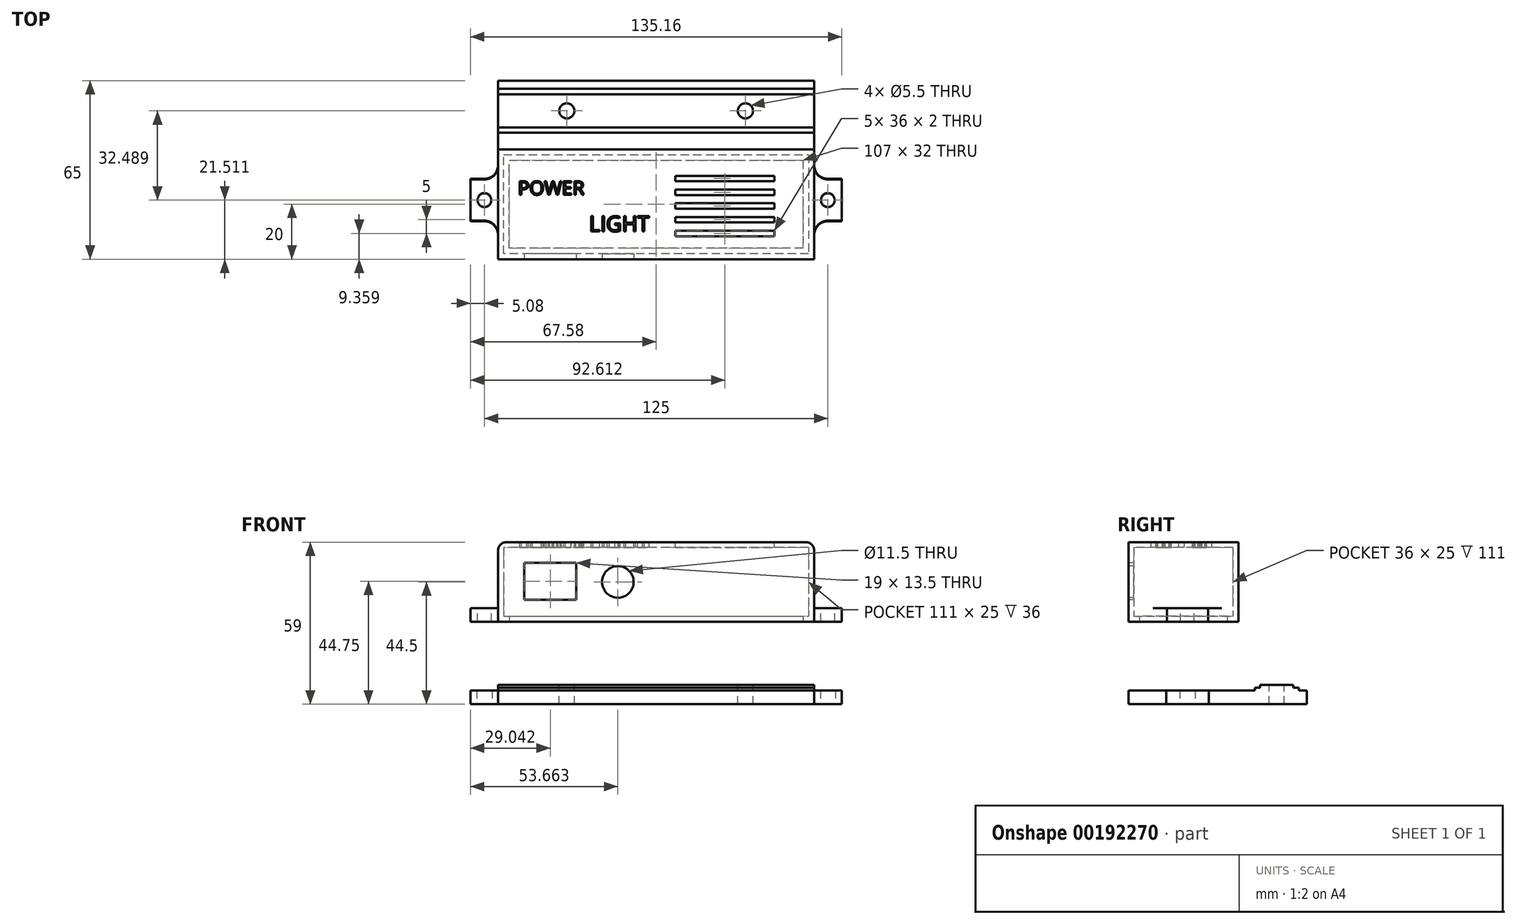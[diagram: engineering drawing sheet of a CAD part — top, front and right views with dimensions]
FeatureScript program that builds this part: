
annotation { "Feature Type Name" : "Feature", "Feature Type Description" : "" }
export const myFeature = defineFeature(function(context is Context, id is Id, definition is map)
    precondition{}
    {
        {
            var Q0;
            Q0=qCreatedBy(makeId("Top.planeOp"),FACE);
            var sketch = newSketch(context, id + "F0", { "sketchPlane" : qUnion([Q0])});
            skLineSegment(sketch, "E0", {"start": v(0, 0) * mm, "end": v(0, 40) * mm});
            skLineSegment(sketch, "E1", {"start": v(0, 40) * mm, "end": v(115, 40) * mm});
            skLineSegment(sketch, "E2", {"start": v(115, 40) * mm, "end": v(115, 0) * mm});
            skLineSegment(sketch, "E3", {"start": v(115, 0) * mm, "end": v(0, 0) * mm});
            skPoint(sketch, "E4.endSnap0", {"position": v(0, 20) * mm});
            skLineSegment(sketch, "E5", {"start": v(-10, 20) * mm, "end": v(-10, 29) * mm});
            skLineSegment(sketch, "E6", {"start": v(-10, 29) * mm, "end": v(0, 29) * mm});
            skLineSegment(sketch, "E7", {"start": v(0, 29) * mm, "end": v(0, 14) * mm});
            skLineSegment(sketch, "E8", {"start": v(0, 14) * mm, "end": v(-10, 14) * mm});
            skLineSegment(sketch, "E9", {"start": v(-10, 14) * mm, "end": v(-10, 20) * mm});
            skLineSegment(sketch, "E10", {"start": v(125, 15) * mm, "end": v(125, 29) * mm});
            skLineSegment(sketch, "E11", {"start": v(125, 29) * mm, "end": v(115, 29) * mm});
            skLineSegment(sketch, "E12", {"start": v(115, 29) * mm, "end": v(115, 14) * mm});
            skLineSegment(sketch, "E13", {"start": v(115, 14) * mm, "end": v(125, 14) * mm});
            skLineSegment(sketch, "E14", {"start": v(125, 14) * mm, "end": v(125, 15) * mm});
            skLineSegment(sketch, "E15.0", {"start": v(2, 2) * mm, "end": v(2, 38) * mm});
            skLineSegment(sketch, "E15.1", {"start": v(113, 2) * mm, "end": v(2, 2) * mm});
            skLineSegment(sketch, "E15.2", {"start": v(113, 38) * mm, "end": v(113, 2) * mm});
            skLineSegment(sketch, "E15.3", {"start": v(2, 38) * mm, "end": v(113, 38) * mm});
            skSolve(sketch);
        }
        {
            var Q0;
            {var subQ5=sQuery(id+"F0.wireOp",EDGE,"E1");Q0=makeQuery(id+"F0.imprint","IMPRINT",FACE,{"disambiguationData":[TD([[makeQuery(id+"F0.imprint","IMPRINT",EDGE,{"derivedFrom":subQ5}),-1.0]])]});}
            extrude(context, id + "F1", {"entities" : qUnion([Q0]), "depth" : 25 * mm});
        }
        {
            var Q0;
            Q0=makeQuery(id+"F0.imprint","IMPRINT",FACE,{"disambiguationData":[TD([[makeQuery(id+"F0.imprint","IMPRINT",EDGE,{"derivedFrom":sQuery(id+"F0.wireOp",EDGE,"E5")}),-1.0]])]});
            var Q1;
            Q1=makeQuery(id+"F0.imprint","IMPRINT",FACE,{"disambiguationData":[TD([[makeQuery(id+"F0.imprint","IMPRINT",EDGE,{"derivedFrom":sQuery(id+"F0.wireOp",EDGE,"E10")}),1.0]])]});
            extrude(context, id + "F2", {"entities" : qUnion([Q0, Q1]), "operationType" : NewBodyOperationType.ADD, "depth" : 3 * mm});
        }
        {
            var Q0;
            Q0=makeQuery(id+"F1.opExtrude","CAP_FACE",FACE,{"disambiguationData":[OSD([sQuery(id+"F0.wireOp",EDGE,"E0"),sQuery(id+"F0.wireOp",EDGE,"E1"),sQuery(id+"F0.wireOp",EDGE,"E2"),sQuery(id+"F0.wireOp",EDGE,"E3"),sQuery(id+"F0.wireOp",EDGE,"E7"),sQuery(id+"F0.wireOp",EDGE,"E12"),sQuery(id+"F0.wireOp",EDGE,"E15.0"),sQuery(id+"F0.wireOp",EDGE,"E15.1"),sQuery(id+"F0.wireOp",EDGE,"E15.2"),sQuery(id+"F0.wireOp",EDGE,"E15.3")])],"isStart":false});
            var sketch = newSketch(context, id + "F3", { "sketchPlane" : qUnion([Q0])});
            skLineSegment(sketch, "E16", {"start": v(0, 40) * mm, "end": v(115, 40) * mm});
            skLineSegment(sketch, "E17", {"start": v(115, 40) * mm, "end": v(115, 0) * mm});
            skLineSegment(sketch, "E18", {"start": v(115, 0) * mm, "end": v(0, 0) * mm});
            skLineSegment(sketch, "E19", {"start": v(0, 0) * mm, "end": v(0, 40) * mm});
            skSolve(sketch);
        }
        {
            var Q0;
            Q0 = qSketchRegion(id + "F3", true);
            extrude(context, id + "F4", {"entities" : qUnion([Q0]), "operationType" : NewBodyOperationType.ADD, "depth" : 2 * mm});
        }
        {
            var Q0;
            {var subQ0=sQuery(id+"F0.wireOp",EDGE,"E12");var subQ1=sQuery(id+"F0.wireOp",EDGE,"E7");Q0=makeQuery(id+"F2.boolean.opBoolean","MERGE",FACE,{"derivedFrom":[makeQuery(id+"F1.opExtrude","CAP_FACE",FACE,{"disambiguationData":[OSD([sQuery(id+"F0.wireOp",EDGE,"E0"),sQuery(id+"F0.wireOp",EDGE,"E1"),sQuery(id+"F0.wireOp",EDGE,"E2"),sQuery(id+"F0.wireOp",EDGE,"E3"),subQ1,subQ0,sQuery(id+"F0.wireOp",EDGE,"E15.0"),sQuery(id+"F0.wireOp",EDGE,"E15.1"),sQuery(id+"F0.wireOp",EDGE,"E15.2"),sQuery(id+"F0.wireOp",EDGE,"E15.3")])],"isStart":true}),makeQuery(id+"F2.opExtrude","CAP_FACE",FACE,{"disambiguationData":[OSD([sQuery(id+"F0.wireOp",EDGE,"E5"),sQuery(id+"F0.wireOp",EDGE,"E6"),subQ1,sQuery(id+"F0.wireOp",EDGE,"E8"),sQuery(id+"F0.wireOp",EDGE,"E9")])],"isStart":true}),makeQuery(id+"F2.opExtrude","CAP_FACE",FACE,{"disambiguationData":[OSD([sQuery(id+"F0.wireOp",EDGE,"E10"),sQuery(id+"F0.wireOp",EDGE,"E11"),subQ0,sQuery(id+"F0.wireOp",EDGE,"E13"),sQuery(id+"F0.wireOp",EDGE,"E14")])],"isStart":true})]});}
            var sketch = newSketch(context, id + "F5", { "sketchPlane" : qUnion([Q0])});
            skLineSegment(sketch, "E20", {"start": v(0, 0) * mm, "end": v(115, 0) * mm});
            skLineSegment(sketch, "E21", {"start": v(115, 0) * mm, "end": v(115, -14) * mm});
            skLineSegment(sketch, "E22", {"start": v(115, -14) * mm, "end": v(125, -14) * mm});
            skLineSegment(sketch, "E23", {"start": v(125, -14) * mm, "end": v(125, -29) * mm});
            skLineSegment(sketch, "E24", {"start": v(125, -29) * mm, "end": v(115, -29) * mm});
            skLineSegment(sketch, "E25", {"start": v(115, -29) * mm, "end": v(115, -40) * mm});
            skLineSegment(sketch, "E26", {"start": v(115, -40) * mm, "end": v(0, -40) * mm});
            skLineSegment(sketch, "E27", {"start": v(0, -40) * mm, "end": v(0, -29) * mm});
            skLineSegment(sketch, "E28", {"start": v(0, -29) * mm, "end": v(-10, -29) * mm});
            skLineSegment(sketch, "E29", {"start": v(-10, -29) * mm, "end": v(-10, -14) * mm});
            skLineSegment(sketch, "E30", {"start": v(-10, -14) * mm, "end": v(0, -14) * mm});
            skLineSegment(sketch, "E31", {"start": v(0, -14) * mm, "end": v(0, 0) * mm});
            skSolve(sketch);
        }
        {
            var Q0;
            Q0 = qSketchRegion(id + "F5", true);
            extrude(context, id + "F6", {"entities" : qUnion([Q0]), "operationType" : NewBodyOperationType.ADD, "depth" : 2 * mm});
        }
        {
            var Q0;
            Q0=makeQuery(id+"F2.opExtrude","CAP_FACE",FACE,{"disambiguationData":[OSD([sQuery(id+"F0.wireOp",EDGE,"E5"),sQuery(id+"F0.wireOp",EDGE,"E6"),sQuery(id+"F0.wireOp",EDGE,"E7"),sQuery(id+"F0.wireOp",EDGE,"E8"),sQuery(id+"F0.wireOp",EDGE,"E9")])],"isStart":false});
            var sketch = newSketch(context, id + "F7", { "sketchPlane" : qUnion([Q0])});
            skCircle(sketch, "E32", {"center": v(-5, 21.5) * mm, "radius": 2.5 * mm});
            skPoint(sketch, "E32.centerSnap0", {"position": v(-5, 14) * mm});
            skPoint(sketch, "E32.centerSnap1", {"position": v(-10, 21.5) * mm});
            skSolve(sketch);
        }
        {
            var Q0;
            Q0 = qSketchRegion(id + "F7", true);
            extrude(context, id + "F8", {"entities" : qUnion([Q0]), "operationType" : NewBodyOperationType.REMOVE, "oppositeDirection" : true, "depth" : 10 * mm});
        }
        {
            var Q0;
            Q0=makeQuery(id+"F2.opExtrude","CAP_FACE",FACE,{"disambiguationData":[OSD([sQuery(id+"F0.wireOp",EDGE,"E10"),sQuery(id+"F0.wireOp",EDGE,"E11"),sQuery(id+"F0.wireOp",EDGE,"E12"),sQuery(id+"F0.wireOp",EDGE,"E13"),sQuery(id+"F0.wireOp",EDGE,"E14")])],"isStart":false});
            var sketch = newSketch(context, id + "F9", { "sketchPlane" : qUnion([Q0])});
            skCircle(sketch, "E33", {"center": v(120, 21.5) * mm, "radius": 2.5 * mm});
            skPoint(sketch, "E33.centerSnap0", {"position": v(125, 21.5) * mm});
            skPoint(sketch, "E33.centerSnap1", {"position": v(120, 14) * mm});
            skSolve(sketch);
        }
        {
            var Q0;
            Q0 = qSketchRegion(id + "F9", true);
            extrude(context, id + "F10", {"entities" : qUnion([Q0]), "operationType" : NewBodyOperationType.REMOVE, "oppositeDirection" : true, "depth" : 10 * mm});
        }
        {
            var Q0;
            Q0=makeQuery(id+"F6.boolean.opBoolean","MERGE",FACE,{"derivedFrom":[makeQuery(id+"F4.boolean.opBoolean","MERGE",FACE,{"derivedFrom":[makeQuery(id+"F1.opExtrude","SWEPT_FACE",FACE,{"disambiguationData":[OSD([sQuery(id+"F0.wireOp",EDGE,"E3")])]}),makeQuery(id+"F4.opExtrude","SWEPT_FACE",FACE,{"disambiguationData":[OSD([sQuery(id+"F3.wireOp",EDGE,"E18")])]})]}),makeQuery(id+"F6.opExtrude","SWEPT_FACE",FACE,{"disambiguationData":[OSD([sQuery(id+"F5.wireOp",EDGE,"E20")])]})]});
            var sketch = newSketch(context, id + "F11", { "sketchPlane" : qUnion([Q0])});
            skLineSegment(sketch, "E34", {"start": v(18.46, 19.5) * mm, "end": v(9.46, 19.5) * mm});
            skLineSegment(sketch, "E35", {"start": v(9.46, 19.5) * mm, "end": v(9.46, 6) * mm});
            skLineSegment(sketch, "E36", {"start": v(9.46, 6) * mm, "end": v(28.46, 6) * mm});
            skLineSegment(sketch, "E37", {"start": v(28.46, 6) * mm, "end": v(28.46, 19.5) * mm});
            skLineSegment(sketch, "E38", {"start": v(28.46, 19.5) * mm, "end": v(18.46, 19.5) * mm});
            skSolve(sketch);
        }
        {
            var Q0;
            Q0 = qSketchRegion(id + "F11", true);
            extrude(context, id + "F12", {"entities" : qUnion([Q0]), "operationType" : NewBodyOperationType.REMOVE, "oppositeDirection" : true, "depth" : 5 * mm});
        }
        {
            var Q0;
            Q0=makeQuery(id+"F6.boolean.opBoolean","MERGE",FACE,{"derivedFrom":[makeQuery(id+"F4.boolean.opBoolean","MERGE",FACE,{"derivedFrom":[makeQuery(id+"F1.opExtrude","SWEPT_FACE",FACE,{"disambiguationData":[OSD([sQuery(id+"F0.wireOp",EDGE,"E3")])]}),makeQuery(id+"F4.opExtrude","SWEPT_FACE",FACE,{"disambiguationData":[OSD([sQuery(id+"F3.wireOp",EDGE,"E18")])]})]}),makeQuery(id+"F6.opExtrude","SWEPT_FACE",FACE,{"disambiguationData":[OSD([sQuery(id+"F5.wireOp",EDGE,"E20")])]})]});
            var sketch = newSketch(context, id + "F13", { "sketchPlane" : qUnion([Q0])});
            skPoint(sketch, "E39.endSnap0", {"position": v(0, 12.5) * mm});
            skCircle(sketch, "E40", {"center": v(43.58, 12.5) * mm, "radius": 5.75 * mm});
            skSolve(sketch);
        }
        {
            var Q0;
            Q0 = qSketchRegion(id + "F13", true);
            extrude(context, id + "F14", {"entities" : qUnion([Q0]), "operationType" : NewBodyOperationType.REMOVE, "oppositeDirection" : true, "depth" : 5 * mm});
        }
        {
            var Q0;
            Q0=makeQuery(id+"F6.boolean.opBoolean","MERGE",EDGE,{"derivedFrom":[makeQuery(id+"F2.opExtrude","SWEPT_EDGE",EDGE,{"disambiguationData":[OSD([sQuery(id+"F0.wireOp",EDGE,"E0"),sQuery(id+"F0.wireOp",EDGE,"E7"),sQuery(id+"F0.wireOp",EDGE,"E8")])]}),makeQuery(id+"F6.opExtrude","SWEPT_EDGE",EDGE,{"disambiguationData":[OSD([sQuery(id+"F5.wireOp",EDGE,"E30"),sQuery(id+"F5.wireOp",EDGE,"E31")])]})]});
            var Q1;
            Q1=makeQuery(id+"F6.boolean.opBoolean","MERGE",EDGE,{"derivedFrom":[makeQuery(id+"F2.opExtrude","SWEPT_EDGE",EDGE,{"disambiguationData":[OSD([sQuery(id+"F0.wireOp",EDGE,"E0"),sQuery(id+"F0.wireOp",EDGE,"E6"),sQuery(id+"F0.wireOp",EDGE,"E7")])]}),makeQuery(id+"F6.opExtrude","SWEPT_EDGE",EDGE,{"disambiguationData":[OSD([sQuery(id+"F5.wireOp",EDGE,"E27"),sQuery(id+"F5.wireOp",EDGE,"E28")])]})]});
            var Q2;
            Q2=makeQuery(id+"F6.boolean.opBoolean","MERGE",EDGE,{"derivedFrom":[makeQuery(id+"F2.opExtrude","SWEPT_EDGE",EDGE,{"disambiguationData":[OSD([sQuery(id+"F0.wireOp",EDGE,"E2"),sQuery(id+"F0.wireOp",EDGE,"E12"),sQuery(id+"F0.wireOp",EDGE,"E13")])]}),makeQuery(id+"F6.opExtrude","SWEPT_EDGE",EDGE,{"disambiguationData":[OSD([sQuery(id+"F5.wireOp",EDGE,"E21"),sQuery(id+"F5.wireOp",EDGE,"E22")])]})]});
            var Q3;
            Q3=makeQuery(id+"F6.boolean.opBoolean","MERGE",EDGE,{"derivedFrom":[makeQuery(id+"F2.opExtrude","SWEPT_EDGE",EDGE,{"disambiguationData":[OSD([sQuery(id+"F0.wireOp",EDGE,"E2"),sQuery(id+"F0.wireOp",EDGE,"E11"),sQuery(id+"F0.wireOp",EDGE,"E12")])]}),makeQuery(id+"F6.opExtrude","SWEPT_EDGE",EDGE,{"disambiguationData":[OSD([sQuery(id+"F5.wireOp",EDGE,"E24"),sQuery(id+"F5.wireOp",EDGE,"E25")])]})]});
            fillet(context, id + "F15", {"entities" : qUnion([Q0, Q1, Q2, Q3]), "radius" : 5 * mm, "tangentPropagation" : true, "allowEdgeOverflow" : false});
        }
        {
            var Q0;
            Q0=makeQuery(id+"F4.opExtrude","CAP_EDGE",EDGE,{"disambiguationData":[OSD([sQuery(id+"F3.wireOp",EDGE,"E19")])],"isStart":false});
            var Q1;
            Q1=makeQuery(id+"F4.opExtrude","CAP_EDGE",EDGE,{"disambiguationData":[OSD([sQuery(id+"F3.wireOp",EDGE,"E17")])],"isStart":false});
            fillet(context, id + "F16", {"entities" : qUnion([Q0, Q1]), "radius" : 3 * mm, "tangentPropagation" : true, "allowEdgeOverflow" : false});
        }
        {
            var Q0;
            Q0=makeQuery(id+"F4.opExtrude","CAP_FACE",FACE,{"disambiguationData":[OSD([sQuery(id+"F3.wireOp",EDGE,"E16"),sQuery(id+"F3.wireOp",EDGE,"E17"),sQuery(id+"F3.wireOp",EDGE,"E18"),sQuery(id+"F3.wireOp",EDGE,"E19")])],"isStart":false});
            var sketch = newSketch(context, id + "F17", { "sketchPlane" : qUnion([Q0])});
            skLineSegment(sketch, "E41", {"start": v(64.53, 30.36) * mm, "end": v(100.53, 30.36) * mm});
            skLineSegment(sketch, "E42", {"start": v(100.53, 30.36) * mm, "end": v(100.53, 28.36) * mm});
            skLineSegment(sketch, "E43", {"start": v(100.53, 28.36) * mm, "end": v(64.53, 28.36) * mm});
            skLineSegment(sketch, "E44", {"start": v(64.53, 25.36) * mm, "end": v(100.53, 25.36) * mm});
            skLineSegment(sketch, "E45", {"start": v(100.53, 25.36) * mm, "end": v(100.53, 23.36) * mm});
            skLineSegment(sketch, "E46", {"start": v(100.53, 23.36) * mm, "end": v(64.53, 23.36) * mm});
            skLineSegment(sketch, "E47", {"start": v(64.53, 20.36) * mm, "end": v(100.53, 20.36) * mm});
            skLineSegment(sketch, "E48", {"start": v(100.53, 20.36) * mm, "end": v(100.53, 18.36) * mm});
            skLineSegment(sketch, "E49", {"start": v(100.53, 18.36) * mm, "end": v(64.53, 18.36) * mm});
            skLineSegment(sketch, "E50", {"start": v(64.53, 15.36) * mm, "end": v(100.53, 15.36) * mm});
            skLineSegment(sketch, "E51", {"start": v(100.53, 15.36) * mm, "end": v(100.53, 13.36) * mm});
            skLineSegment(sketch, "E52", {"start": v(100.53, 13.36) * mm, "end": v(64.53, 13.36) * mm});
            skLineSegment(sketch, "E53", {"start": v(64.53, 10.36) * mm, "end": v(100.53, 10.36) * mm});
            skLineSegment(sketch, "E54", {"start": v(100.53, 10.36) * mm, "end": v(100.53, 8.36) * mm});
            skLineSegment(sketch, "E55", {"start": v(100.53, 8.36) * mm, "end": v(64.53, 8.36) * mm});
            skLineSegment(sketch, "E56", {"start": v(64.53, 30.36) * mm, "end": v(64.53, 28.36) * mm});
            skLineSegment(sketch, "E57", {"start": v(64.53, 25.36) * mm, "end": v(64.53, 23.36) * mm});
            skLineSegment(sketch, "E58", {"start": v(64.53, 20.36) * mm, "end": v(64.53, 18.36) * mm});
            skLineSegment(sketch, "E59", {"start": v(64.53, 15.36) * mm, "end": v(64.53, 13.36) * mm});
            skLineSegment(sketch, "E60", {"start": v(64.53, 10.36) * mm, "end": v(64.53, 8.36) * mm});
            skSolve(sketch);
        }
        {
            var Q0;
            Q0 = qSketchRegion(id + "F17", true);
            extrude(context, id + "F18", {"entities" : qUnion([Q0]), "operationType" : NewBodyOperationType.REMOVE, "oppositeDirection" : true, "depth" : 5 * mm});
        }
        {
            var Q0;
            Q0=makeQuery(id+"F6.opExtrude","CAP_FACE",FACE,{"disambiguationData":[OSD([sQuery(id+"F5.wireOp",EDGE,"E20"),sQuery(id+"F5.wireOp",EDGE,"E21"),sQuery(id+"F5.wireOp",EDGE,"E22"),sQuery(id+"F5.wireOp",EDGE,"E23"),sQuery(id+"F5.wireOp",EDGE,"E24"),sQuery(id+"F5.wireOp",EDGE,"E25"),sQuery(id+"F5.wireOp",EDGE,"E26"),sQuery(id+"F5.wireOp",EDGE,"E27"),sQuery(id+"F5.wireOp",EDGE,"E28"),sQuery(id+"F5.wireOp",EDGE,"E29"),sQuery(id+"F5.wireOp",EDGE,"E30"),sQuery(id+"F5.wireOp",EDGE,"E31")])],"isStart":false});
            var sketch = newSketch(context, id + "F19", { "sketchPlane" : qUnion([Q0])});
            skLineSegment(sketch, "E61", {"start": v(0, 0) * mm, "end": v(0, -40) * mm});
            skLineSegment(sketch, "E62", {"start": v(0, -40) * mm, "end": v(115, -40) * mm});
            skLineSegment(sketch, "E63", {"start": v(115, -40) * mm, "end": v(115, 0) * mm});
            skLineSegment(sketch, "E64", {"start": v(115, 0) * mm, "end": v(0, 0) * mm});
            skLineSegment(sketch, "E65.0", {"start": v(111, -4) * mm, "end": v(4, -4) * mm});
            skLineSegment(sketch, "E65.1", {"start": v(111, -36) * mm, "end": v(111, -4) * mm});
            skLineSegment(sketch, "E65.2", {"start": v(4, -36) * mm, "end": v(111, -36) * mm});
            skLineSegment(sketch, "E65.3", {"start": v(4, -4) * mm, "end": v(4, -36) * mm});
            skSolve(sketch);
        }
        {
            var Q0;
            Q0=makeQuery(id+"F19.imprint","IMPRINT",FACE,{"disambiguationData":[TD([[makeQuery(id+"F19.imprint","IMPRINT",EDGE,{"derivedFrom":sQuery(id+"F19.wireOp",EDGE,"E65.0")}),1.0]])]});
            extrude(context, id + "F20", {"entities" : qUnion([Q0]), "operationType" : NewBodyOperationType.REMOVE, "oppositeDirection" : true, "depth" : 5 * mm});
        }
        {
            var Q0;
            Q0=makeQuery(id+"F4.opExtrude","CAP_FACE",FACE,{"disambiguationData":[OSD([sQuery(id+"F3.wireOp",EDGE,"E16"),sQuery(id+"F3.wireOp",EDGE,"E17"),sQuery(id+"F3.wireOp",EDGE,"E18"),sQuery(id+"F3.wireOp",EDGE,"E19")])],"isStart":false});
            var sketch = newSketch(context, id + "F21", { "sketchPlane" : qUnion([Q0])});
            skText(sketch, "E66", { "text": "POWER", "fontName": "OpenSans-Regular.ttf"});
            skText(sketch, "E67", { "text": "LIGHT\n", "fontName": "OpenSans-Regular.ttf"});
            const initialGuessF21  = {"E66": [0.00721, 0.02342, 1, 0, 0.005], "E67": [0.03308, 0.01007, 1, 0, 0.00562]};
            skSetInitialGuess(sketch, initialGuessF21);
            skSolve(sketch);
        }
        {
            var Q0;
            Q0 = qSketchRegion(id + "F21", true);
            extrude(context, id + "F22", {"entities" : qUnion([Q0]), "operationType" : NewBodyOperationType.REMOVE, "oppositeDirection" : true, "depth" : 5 * mm});
        }
        {
            var Q0;
            Q0=makeQuery(id+"F6.opExtrude","CAP_FACE",FACE,{"disambiguationData":[OSD([sQuery(id+"F5.wireOp",EDGE,"E20"),sQuery(id+"F5.wireOp",EDGE,"E21"),sQuery(id+"F5.wireOp",EDGE,"E22"),sQuery(id+"F5.wireOp",EDGE,"E23"),sQuery(id+"F5.wireOp",EDGE,"E24"),sQuery(id+"F5.wireOp",EDGE,"E25"),sQuery(id+"F5.wireOp",EDGE,"E26"),sQuery(id+"F5.wireOp",EDGE,"E27"),sQuery(id+"F5.wireOp",EDGE,"E28"),sQuery(id+"F5.wireOp",EDGE,"E29"),sQuery(id+"F5.wireOp",EDGE,"E30"),sQuery(id+"F5.wireOp",EDGE,"E31")])],"isStart":false});
            cPlane(context, id + "F23", {"entities" : qUnion([Q0]), "cplaneType" : CPlaneType.OFFSET, "offset" : 25 * mm, "width" : 150 * mm, "height" : 150 * mm});
        }
        {
            var Q0;
            Q0=qCreatedBy(id+"F23.planeOp",FACE);
            var sketch = newSketch(context, id + "F24", { "sketchPlane" : qUnion([Q0])});
            skLineSegment(sketch, "E68.bottom", {"start": v(0, 0) * mm, "end": v(115, 0) * mm});
            skLineSegment(sketch, "E68.top", {"start": v(0, -65) * mm, "end": v(115, -65) * mm});
            skLineSegment(sketch, "E68.left", {"start": v(0, 0) * mm, "end": v(0, -13.76) * mm});
            skLineSegment(sketch, "E68.right", {"start": v(115, 0) * mm, "end": v(115, -13.76) * mm});
            skLineSegment(sketch, "E69.bottom", {"start": v(-10.08, -13.76) * mm, "end": v(0, -13.76) * mm});
            skLineSegment(sketch, "E69.top", {"start": v(-10.08, -29.27) * mm, "end": v(0, -29.27) * mm});
            skLineSegment(sketch, "E69.left", {"start": v(-10.08, -13.76) * mm, "end": v(-10.08, -29.27) * mm});
            skPoint(sketch, "E70.firstSnap0", {"position": v(115, -32.5) * mm});
            skLineSegment(sketch, "E70.bottom", {"start": v(115, -29.27) * mm, "end": v(125.08, -29.27) * mm});
            skLineSegment(sketch, "E70.top", {"start": v(115, -13.76) * mm, "end": v(125.08, -13.76) * mm});
            skLineSegment(sketch, "E70.right", {"start": v(125.08, -29.27) * mm, "end": v(125.08, -13.76) * mm});
            skLineSegment(sketch, "E71.trimOffspring", {"start": v(0, -29.27) * mm, "end": v(0, -65) * mm});
            skLineSegment(sketch, "E72.trimOffspring", {"start": v(115, -29.27) * mm, "end": v(115, -65) * mm});
            skSolve(sketch);
        }
        {
            var Q0;
            Q0=makeQuery(id+"F24.imprint","IMPRINT",FACE,{"disambiguationData":[TD([[makeQuery(id+"F24.imprint","IMPRINT",EDGE,{"derivedFrom":sQuery(id+"F24.wireOp",EDGE,"E68.bottom")}),-1.0]])]});
            extrude(context, id + "F25", {"entities" : qUnion([Q0]), "depth" : 5 * mm});
        }
        {
            var Q0;
            Q0=makeQuery(id+"F25.opExtrude","SWEPT_EDGE",EDGE,{"disambiguationData":[OSD([sQuery(id+"F24.wireOp",EDGE,"E69.top"),sQuery(id+"F24.wireOp",EDGE,"E71.trimOffspring")])]});
            var Q1;
            Q1=makeQuery(id+"F25.opExtrude","SWEPT_EDGE",EDGE,{"disambiguationData":[OSD([sQuery(id+"F24.wireOp",EDGE,"E68.left"),sQuery(id+"F24.wireOp",EDGE,"E69.bottom")])]});
            var Q2;
            Q2=makeQuery(id+"F25.opExtrude","SWEPT_EDGE",EDGE,{"disambiguationData":[OSD([sQuery(id+"F24.wireOp",EDGE,"E70.bottom"),sQuery(id+"F24.wireOp",EDGE,"E72.trimOffspring")])]});
            var Q3;
            Q3=makeQuery(id+"F25.opExtrude","SWEPT_EDGE",EDGE,{"disambiguationData":[OSD([sQuery(id+"F24.wireOp",EDGE,"E68.right"),sQuery(id+"F24.wireOp",EDGE,"E70.top")])]});
            fillet(context, id + "F26", {"entities" : qUnion([Q0, Q1, Q2, Q3]), "radius" : 5 * mm, "tangentPropagation" : true, "allowEdgeOverflow" : false});
        }
        {
            var Q0;
            Q0=makeQuery(id+"F25.opExtrude","CAP_FACE",FACE,{"disambiguationData":[OSD([sQuery(id+"F24.wireOp",EDGE,"E68.bottom"),sQuery(id+"F24.wireOp",EDGE,"E68.top"),sQuery(id+"F24.wireOp",EDGE,"E68.left"),sQuery(id+"F24.wireOp",EDGE,"E68.right"),sQuery(id+"F24.wireOp",EDGE,"E69.bottom"),sQuery(id+"F24.wireOp",EDGE,"E69.top"),sQuery(id+"F24.wireOp",EDGE,"E69.left"),sQuery(id+"F24.wireOp",EDGE,"E70.bottom"),sQuery(id+"F24.wireOp",EDGE,"E70.top"),sQuery(id+"F24.wireOp",EDGE,"E70.right"),sQuery(id+"F24.wireOp",EDGE,"E71.trimOffspring"),sQuery(id+"F24.wireOp",EDGE,"E72.trimOffspring")])],"isStart":false});
            var sketch = newSketch(context, id + "F27", { "sketchPlane" : qUnion([Q0])});
            skCircle(sketch, "E73", {"center": v(-5, -21.51) * mm, "radius": 2.75 * mm});
            skCircle(sketch, "E74", {"center": v(120, -21.51) * mm, "radius": 2.75 * mm});
            skSolve(sketch);
        }
        {
            var Q0;
            Q0 = qSketchRegion(id + "F27", true);
            extrude(context, id + "F28", {"entities" : qUnion([Q0]), "operationType" : NewBodyOperationType.REMOVE, "oppositeDirection" : true, "depth" : 6 * mm});
        }
        {
            var Q0;
            Q0=makeQuery(id+"F25.opExtrude","CAP_FACE",FACE,{"disambiguationData":[OSD([sQuery(id+"F24.wireOp",EDGE,"E68.bottom"),sQuery(id+"F24.wireOp",EDGE,"E68.top"),sQuery(id+"F24.wireOp",EDGE,"E68.left"),sQuery(id+"F24.wireOp",EDGE,"E68.right"),sQuery(id+"F24.wireOp",EDGE,"E69.bottom"),sQuery(id+"F24.wireOp",EDGE,"E69.top"),sQuery(id+"F24.wireOp",EDGE,"E69.left"),sQuery(id+"F24.wireOp",EDGE,"E70.bottom"),sQuery(id+"F24.wireOp",EDGE,"E70.top"),sQuery(id+"F24.wireOp",EDGE,"E70.right"),sQuery(id+"F24.wireOp",EDGE,"E71.trimOffspring"),sQuery(id+"F24.wireOp",EDGE,"E72.trimOffspring")])],"isStart":true});
            var sketch = newSketch(context, id + "F29", { "sketchPlane" : qUnion([Q0])});
            skLineSegment(sketch, "E75", {"start": v(0, 62) * mm, "end": v(115, 62) * mm});
            skLineSegment(sketch, "E76", {"start": v(115, 60) * mm, "end": v(0, 60) * mm});
            skLineSegment(sketch, "E77", {"start": v(0, 48) * mm, "end": v(115, 48) * mm});
            skLineSegment(sketch, "E78", {"start": v(115, 46) * mm, "end": v(0, 46) * mm});
            skSolve(sketch);
        }
        {
            var Q0;
            {var subQ0=sQuery(id+"F29.wireOp",EDGE,"E75");Q0=makeQuery(id+"F29.imprint","IMPRINT",FACE,{"disambiguationData":[TD([[makeQuery(id+"F29.imprint","IMPRINT",EDGE,{"derivedFrom":subQ0}),-1.0]])]});}
            var Q1;
            {var subQ0=sQuery(id+"F29.wireOp",EDGE,"E77");Q1=makeQuery(id+"F29.imprint","IMPRINT",FACE,{"disambiguationData":[TD([[makeQuery(id+"F29.imprint","IMPRINT",EDGE,{"derivedFrom":subQ0}),-1.0]])]});}
            extrude(context, id + "F30", {"entities" : qUnion([Q0, Q1]), "operationType" : NewBodyOperationType.ADD, "depth" : 1 * mm});
        }
        {
            var Q0;
            {var subQ0=sQuery(id+"F29.wireOp",EDGE,"E76");Q0=makeQuery(id+"F29.imprint","IMPRINT",FACE,{"disambiguationData":[TD([[makeQuery(id+"F29.imprint","IMPRINT",EDGE,{"derivedFrom":subQ0}),1.0]])]});}
            extrude(context, id + "F31", {"entities" : qUnion([Q0]), "operationType" : NewBodyOperationType.ADD, "depth" : 2 * mm});
        }
        {
            var Q0;
            Q0=makeQuery(id+"F31.opExtrude","CAP_FACE",FACE,{"disambiguationData":[OSD([sQuery(id+"F24.wireOp",EDGE,"E71.trimOffspring"),sQuery(id+"F24.wireOp",EDGE,"E72.trimOffspring"),sQuery(id+"F29.wireOp",EDGE,"E76"),sQuery(id+"F29.wireOp",EDGE,"E77")])],"isStart":false});
            var sketch = newSketch(context, id + "F32", { "sketchPlane" : qUnion([Q0])});
            skCircle(sketch, "E79", {"center": v(25, 54) * mm, "radius": 2.75 * mm});
            skCircle(sketch, "E80", {"center": v(90, 54) * mm, "radius": 2.75 * mm});
            skSolve(sketch);
        }
        {
            var Q0;
            Q0=makeQuery(id+"F32.imprint","IMPRINT",FACE,{"disambiguationData":[TD([[makeQuery(id+"F32.imprint","IMPRINT",EDGE,{"derivedFrom":sQuery(id+"F32.wireOp",EDGE,"E80")}),1.0]])]});
            var Q1;
            Q1=makeQuery(id+"F32.imprint","IMPRINT",FACE,{"disambiguationData":[TD([[makeQuery(id+"F32.imprint","IMPRINT",EDGE,{"derivedFrom":sQuery(id+"F32.wireOp",EDGE,"E79")}),1.0]])]});
            extrude(context, id + "F33", {"entities" : qUnion([Q0, Q1]), "operationType" : NewBodyOperationType.REMOVE, "oppositeDirection" : true, "depth" : 10 * mm});
        }
    });
